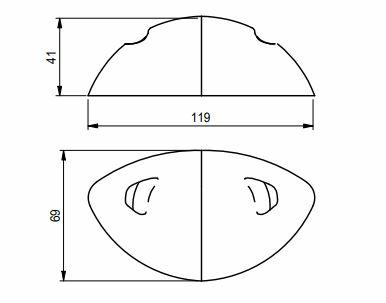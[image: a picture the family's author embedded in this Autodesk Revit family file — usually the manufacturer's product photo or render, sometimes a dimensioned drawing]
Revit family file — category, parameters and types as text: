
# Revit family: R-MBD-482
name_source: partatom
category: Portes
units: mm (PartAtom-declared; Revit-internal decimal feet)

## family parameters
Couper avec des vides une fois chargée = Non
Hôte = Mur
Partagée = Non
Repère de localisation dans la pièce = Oui
Toujours verticalement = Oui

## types (1)
- MBD-482
    1 Vantail = Non
    2 Vantaux = Oui
    A.E.V = non
    Acoustique = non
    Anti-Effraction = non
    Certification = D.A.S. Mode 2 certifié NF
    Code_MAJ = 2303130305MBD482
    Coloris_Chants = BER
    Coloris_Dormant = Hêtre
    Coloris_Face_Cote_Oppose_Ouverture = Prépeint
    Coloris_Face_Cote_Ouverture = Prépeint
    Construction analytique = <Aucun>
    DAS = Oui
    DC Larg Feuillure = 12 mm  [stored 0.0393701 ft]
    DC Pivot Vantail = 60 mm  [stored 0.19685 ft]
    Description = Bloc-porte bois D.A.S. 2 vantaux SP51 avec pivots linteaux motorisés encastrés, double action / va-et-vient, EI60, D.A.S. certifié NF, sur huisserie bois
    Définir les propriétés thermiques par = Type schématique
    Ep Profil Pose Tunnel = 118 mm
    Ep Strat Vantail = 1 mm  [stored 0.00328084 ft]
    Ep Vantail = 51 mm  [stored 0.167323 ft]
    Epaisseur_Rainure à brique = 8 mm  [stored 0.0262467 ft]
    Fabricant = MALERBA
    Fiche_Produit = MBD-482
    Fileur = Non
    Hauteur_Tableau = 2125 mm
    Hauteur_Vantaux_Souhaitée = 2040 mm  [stored 6.69291 ft]
    Jeu_1 = 0 mm  [stored 0 ft]
    Jeu_2 = 0 mm  [stored 0 ft]
    Jeu_Côté_Articulation_Vantail = 8 mm  [stored 0.0262467 ft]
    Jeu_Côté_Fermeture_Vantail = 8 mm  [stored 0.0262467 ft]
    Jeu_Haut = 3 mm  [stored 0.00984252 ft]
    Larg Profil = 58 mm  [stored 0.190289 ft]
    Larg Profil Avec Fileur = 20 mm  [stored 0.0656168 ft]
    Larg Profil Trav = 76 mm  [stored 0.249344 ft]
    Largeur = 0 mm  [stored 0 ft]
    Largeur_Vantail_Semi_Fixe_Souhaitée = 930 mm  [stored 3.05118 ft]
    Largeur_Vantail_Service_Souhaitée = 930 mm  [stored 3.05118 ft]
    Mat APD = Caoutchouc noir
    Mat Parclose = BER 2
    Mat Parclose Métal = Peinture Laquée PMT - Blanc Pur - RAL 9010
    Materiaux_Dominant = Bois
    Modèle = Va et vient
    Montant_VV = Oui
    Note d'identification = 2V EI60/SP51 DAS - LINTEAU MOTORISE - HUISSERIE BOIS
    Pivot linteau motorisé = Oui
    Profondeur_Rainure à brique = 5 mm  [stored 0.0164042 ft]
    Reference_Commerciale = 2V SP51/DA LINTEAU OP
    Resistance_Feu = EI30
    Sans_Montants = Non
    Sens_Feu = Recto / Verso
    Thermique (W/m2.°K) = 0
    URL = https://www.malerba.fr
    X_Axe Pivot = 114 mm  [stored 0.374016 ft]
    X_DC seuil = 9 mm  [stored 0.0295276 ft]
    X_Inv_DC Larg Feuillure_1V Montant = 0 mm  [stored 0 ft]

note: [stored X ft] marks values corroborated as IEEE doubles in the binary element streams (Revit-internal decimal feet)

## geometry (parser evidence)
native form markers: Blend x14
no freeform markers — native parametric forms only
